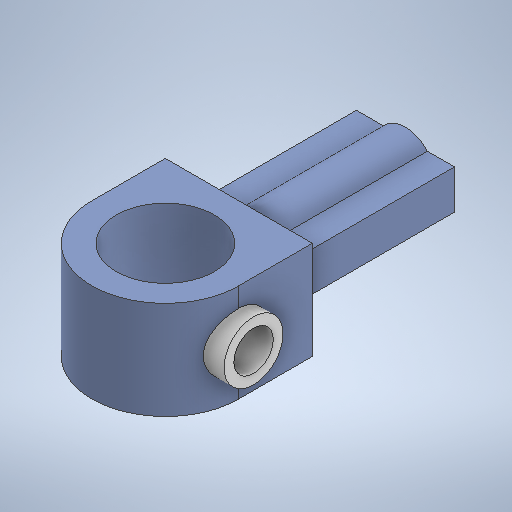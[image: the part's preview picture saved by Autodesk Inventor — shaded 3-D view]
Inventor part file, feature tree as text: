
AUTODESK INVENTOR PART (.ipt)
format: ipt  version: 2025.1 (Build 291241000, 241)  size: 296,448 bytes
history: native  units: in
note: dims shown in document units (in); Inventor stores cm internally (conversion verified against a paired STEP export)
features: extrude x4, sketch x4, other x1
ambient origin geometry x8: Origin, YZ Plane, XZ Plane, XY Plane, X Axis, Y Axis, Z Axis, Center Point
bodies: Solid1 (feature_tree)
feature tree (9):
  extrude  "Extrusion1"  Depth=0.315in
  extrude  "Extrusion2"  Depth=0.315in
  extrude  "Extrusion3"  Depth=0.2953in
  extrude  "Extrusion4"  Depth=0.0591in TaperAngle=0.0deg
  sketch  "Sketch1"  dims[d0=0.315in d1=0.2362in]
  sketch  "Sketch2"  dims[d2=0.315in d3=0.1969in]
  sketch  "Sketch3"  dims[d4=0.2953in d5=0.2953in]
  sketch  "Sketch4"  dims[d6=0.3346in d7=0.1969in d8=0.0in d9=0.1181in d10=0.1969in d11=0.0787in d12=0.3346in d13=0.0in d14=0.1181in d15=0.0591in d16=0.0in d17=0.0787in d18=0.1284in d19=0.0in]
  other  "Finish1"
